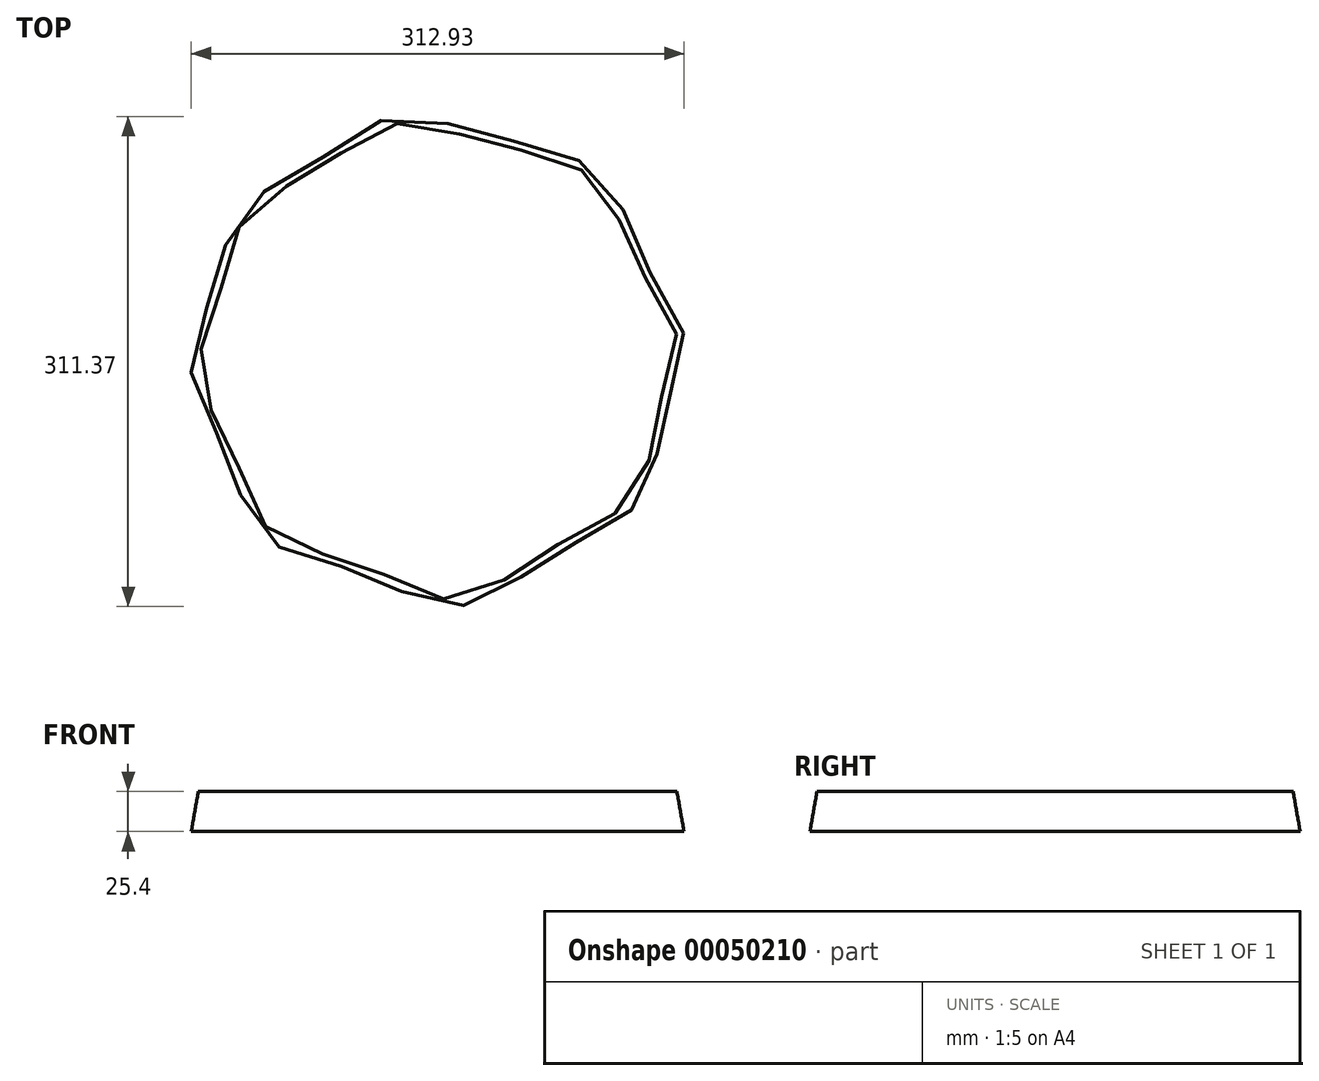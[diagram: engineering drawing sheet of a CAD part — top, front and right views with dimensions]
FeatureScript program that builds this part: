
annotation { "Feature Type Name" : "Feature", "Feature Type Description" : "" }
export const myFeature = defineFeature(function(context is Context, id is Id, definition is map)
    precondition{}
    {
        {
            var Q0;
            Q0=qCreatedBy(makeId("Top.planeOp"),FACE);
            var sketch = newSketch(context, id + "F0", { "sketchPlane" : qUnion([Q0])});
            skCircle(sketch, "E0", {"center": v(0, 0) * mm, "radius": 152.4 * mm, "construction": true});
            skFitSpline(sketch, "E1", {"points": [v(-152.04, -10.5) * mm, v(-134.83, 54.68) * mm, v(-121.55, 91.94) * mm, v(-71.91, 124.34) * mm, v(-28.92, 149.63) * mm, v(31.46, 138.58) * mm, v(102.37, 112.9) * mm, v(124.35, 64.42) * mm, v(151.48, 16.7) * mm, v(138.58, -34.46) * mm, v(127.51, -83.47) * mm, v(74.16, -118.36) * mm, v(10.75, -152.02) * mm, v(-47.94, -130.34) * mm, v(-106.94, -108.58) * mm, v(-132.59, -51.69) * mm, v(-152.04, -10.5) * mm]});
            skSolve(sketch);
        }
        {
            var Q0;
            Q0 = qSketchRegion(id + "F0", true);
            extrude(context, id + "F1", {"entities" : qUnion([Q0]), "oppositeDirection" : true, "depth" : 25.4 * mm, "hasDraft" : true, "draftAngle" : 10 * degree});
        }
    });
